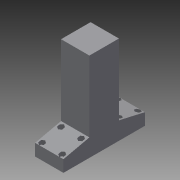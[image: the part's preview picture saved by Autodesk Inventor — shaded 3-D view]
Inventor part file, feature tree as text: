
AUTODESK INVENTOR PART (.ipt)
format: ipt  version: 2015 SP1 (Build 190203100, 203)  size: 189,440 bytes
history: native  units: mm
features: extrude x3, sketch x3, projected_geometry x2, plane x1
ambient origin geometry x8: Origin, YZ Plane, XZ Plane, XY Plane, X Axis, Y Axis, Z Axis, Center Point
bodies: Solid1 (feature_tree)
feature tree (9):
  extrude  "Extrusion1"  Depth=150.0mm
  extrude  "Extrusion2"  Depth=50.0mm
  plane  "Work Plane1"
  extrude  "Extrusion3"  Depth=48.0mm TaperAngle=0.0deg
  sketch  "Sketch1"  dims[d0=138.0mm d1=150.0mm]
  sketch  "Sketch2"  dims[d2=50.0mm d3=120.0mm]
  sketch  "Sketch3"  dims[d4=20.0mm d5=48.0mm d6=0.0mm d7=32.0mm d8=5.5mm d9=5.0mm d10=34.0mm d11=148.0mm d12=0.0mm d13=-15.0mm d14=5.0mm d15=148.0mm d16=0.0mm]
  projected_geometry  "Projected Loop1"
  projected_geometry  "Projected Loop2"
